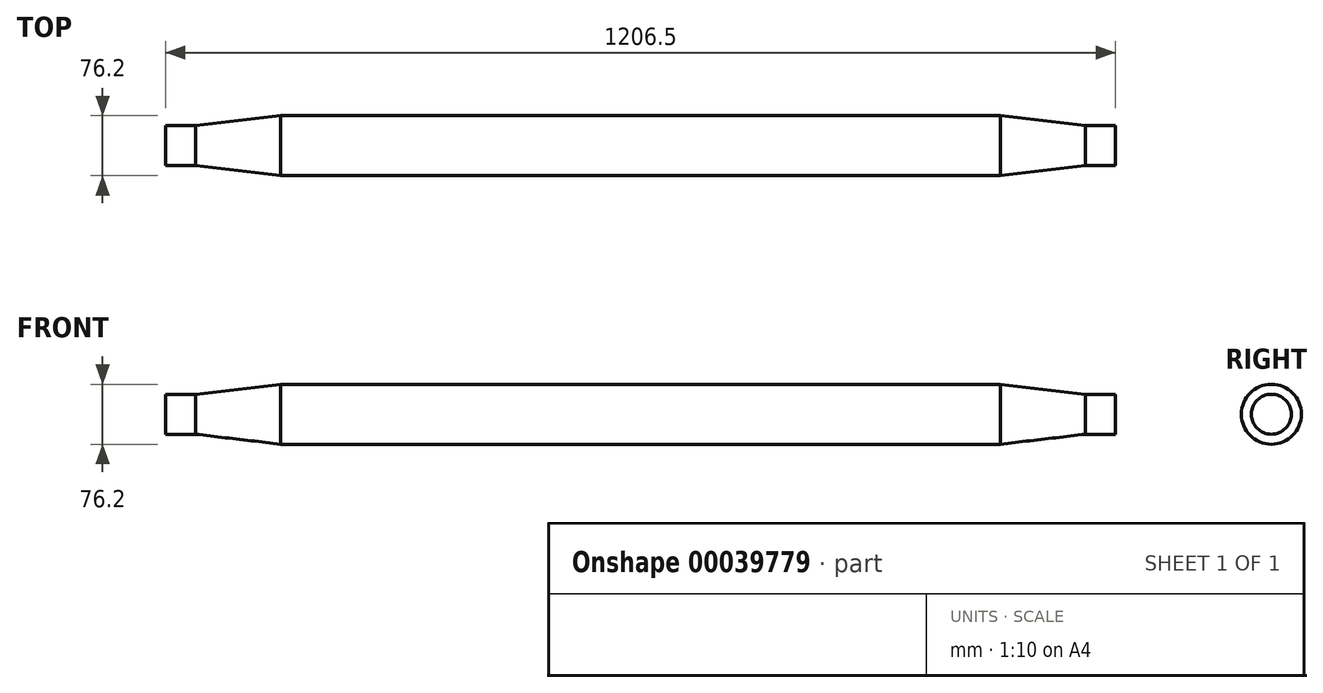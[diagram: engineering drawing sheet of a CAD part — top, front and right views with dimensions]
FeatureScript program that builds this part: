
annotation { "Feature Type Name" : "Feature", "Feature Type Description" : "" }
export const myFeature = defineFeature(function(context is Context, id is Id, definition is map)
    precondition{}
    {
        {
            var Q0;
            Q0=qCreatedBy(makeId("Right.planeOp"),FACE);
            var sketch = newSketch(context, id + "F0", { "sketchPlane" : qUnion([Q0])});
            skCircle(sketch, "E0", {"center": v(0, 0) * mm, "radius": 38.1 * mm});
            skSolve(sketch);
        }
        {
            var Q0;
            Q0 = qSketchRegion(id + "F0", true);
            extrude(context, id + "F1", {"entities" : qUnion([Q0]), "endBound" : BoundingType.SYMMETRIC, "depth" : 914.4 * mm});
        }
        {
            var Q0;
            Q0=makeQuery(id+"F1.opExtrude","CAP_FACE",FACE,{"disambiguationData":[OSD([sQuery(id+"F0.wireOp",EDGE,"E0")])],"isStart":false});
            cPlane(context, id + "F2", {"entities" : qUnion([Q0]), "cplaneType" : CPlaneType.OFFSET, "offset" : 107.95 * mm, "width" : 152.4 * mm, "height" : 152.4 * mm});
        }
        {
            var Q0;
            Q0=qCreatedBy(id+"F2.planeOp",FACE);
            var sketch = newSketch(context, id + "F3", { "sketchPlane" : qUnion([Q0])});
            skCircle(sketch, "E1", {"center": v(0, 0) * mm, "radius": 25.4 * mm});
            skSolve(sketch);
        }
        {
            var Q0;
            Q0 = qSketchRegion(id + "F3", true);
            extrude(context, id + "F4", {"entities" : qUnion([Q0]), "depth" : 38.1 * mm});
        }
        {
            var Q0;
            Q0=makeQuery(id+"F1.opExtrude","CAP_FACE",FACE,{"disambiguationData":[OSD([sQuery(id+"F0.wireOp",EDGE,"E0")])],"isStart":false});
            var Q1;
            Q1=makeQuery(id+"F4.opExtrude","CAP_FACE",FACE,{"disambiguationData":[OSD([sQuery(id+"F3.wireOp",EDGE,"E1")])],"isStart":true});
            loft(context, id + "F5", {"sheetProfilesArray" : [{ "sheetProfileEntities" : qUnion([Q0]) }, { "sheetProfileEntities" : qUnion([Q1]) }]});
        }
        {
            var Q0;
            Q0=makeQuery(id+"F4.opExtrude","SWEPT_BODY",BODY,{"disambiguationData":[OSD([sQuery(id+"F3.wireOp",EDGE,"E1")])]});
            var Q1;
            Q1=makeQuery(id+"F5.opLoft","SWEPT_BODY",BODY,{"disambiguationData":[OSD([sQuery(id+"F0.wireOp",EDGE,"E0"),sQuery(id+"F3.wireOp",EDGE,"E1")])]});
            var Q2;
            Q2=qCreatedBy(makeId("Right.planeOp"),FACE);
            mirror(context, id + "F6", {"operationType" : NewBodyOperationType.ADD, "entities" : qUnion([Q0, Q1]), "mirrorPlane" : qUnion([Q2])});
        }
    });
